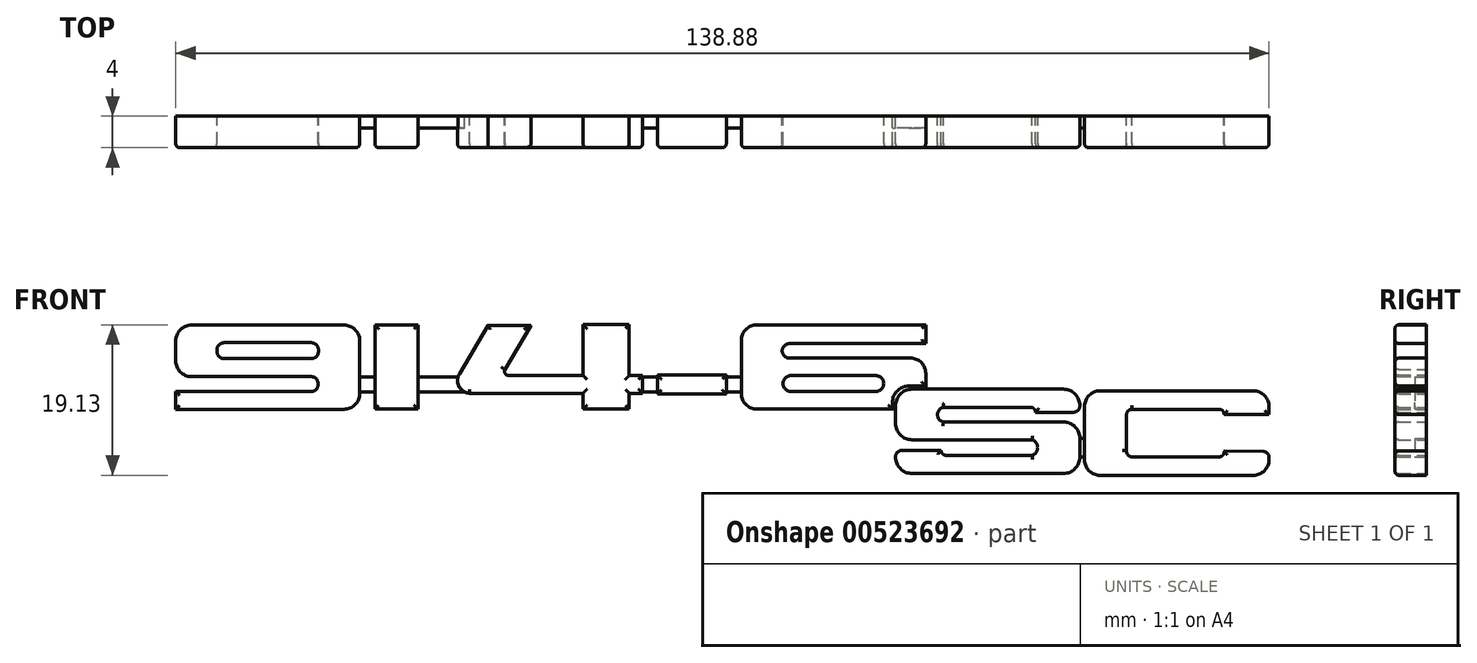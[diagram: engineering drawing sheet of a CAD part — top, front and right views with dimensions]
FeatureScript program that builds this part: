
annotation { "Feature Type Name" : "Feature", "Feature Type Description" : "" }
export const myFeature = defineFeature(function(context is Context, id is Id, definition is map)
    precondition{}
    {
        {
            var Q0;
            Q0=qCreatedBy(makeId("Front.planeOp"),FACE);
            var sketch = newSketch(context, id + "F0", { "sketchPlane" : qUnion([Q0])});
            skLineSegment(sketch, "E0.bottom", {"start": v(-66.52, 34.25) * mm, "end": v(-47.14, 34.25) * mm});
            skLineSegment(sketch, "E0.top", {"start": v(-68.52, 23.57) * mm, "end": v(-47.14, 23.57) * mm});
            skLineSegment(sketch, "E0.left", {"start": v(-68.52, 32.25) * mm, "end": v(-68.52, 29.72) * mm});
            skLineSegment(sketch, "E0.right", {"start": v(-45.14, 32.25) * mm, "end": v(-45.14, 25.57) * mm});
            skPoint(sketch, "E1.visualSharp", {"position": v(-68.52, 34.25) * mm});
            skArc(sketch, "E1.filletArc", {"start": v(-66.52, 34.25) * mm, "mid": v(-67.93, 33.67) * mm, "end": v(-68.52, 32.25) * mm});
            skLineSegment(sketch, "E2", {"start": v(-66.52, 27.72) * mm, "end": v(-51.34, 27.72) * mm});
            skLineSegment(sketch, "E3", {"start": v(-50.44, 26.81) * mm, "end": v(-50.44, 26.71) * mm});
            skLineSegment(sketch, "E4", {"start": v(-51.34, 25.81) * mm, "end": v(-68.52, 25.81) * mm});
            skLineSegment(sketch, "E5.bottom", {"start": v(-62.39, 32.02) * mm, "end": v(-51.29, 32.02) * mm});
            skLineSegment(sketch, "E5.top", {"start": v(-62.39, 30) * mm, "end": v(-51.29, 30) * mm});
            skLineSegment(sketch, "E5.left", {"start": v(-63.3, 31.12) * mm, "end": v(-63.3, 30.91) * mm});
            skLineSegment(sketch, "E5.right", {"start": v(-50.39, 31.12) * mm, "end": v(-50.39, 30.91) * mm});
            skLineSegment(sketch, "E6.trimOffspring", {"start": v(-68.52, 25.81) * mm, "end": v(-68.52, 23.57) * mm});
            skPoint(sketch, "E7.visualSharp", {"position": v(-68.52, 27.72) * mm});
            skArc(sketch, "E7.filletArc", {"start": v(-68.52, 29.72) * mm, "mid": v(-67.93, 28.3) * mm, "end": v(-66.52, 27.72) * mm});
            skPoint(sketch, "E8.visualSharp", {"position": v(-50.44, 27.72) * mm});
            skArc(sketch, "E8.filletArc", {"start": v(-50.44, 26.81) * mm, "mid": v(-50.7, 27.45) * mm, "end": v(-51.34, 27.72) * mm});
            skPoint(sketch, "E9.visualSharp", {"position": v(-50.44, 25.81) * mm});
            skArc(sketch, "E9.filletArc", {"start": v(-51.34, 25.81) * mm, "mid": v(-50.7, 26.08) * mm, "end": v(-50.44, 26.71) * mm});
            skPoint(sketch, "E10.visualSharp", {"position": v(-63.3, 32.02) * mm});
            skArc(sketch, "E10.filletArc", {"start": v(-62.39, 32.02) * mm, "mid": v(-63.03, 31.75) * mm, "end": v(-63.3, 31.12) * mm});
            skPoint(sketch, "E11.visualSharp", {"position": v(-63.3, 30) * mm});
            skArc(sketch, "E11.filletArc", {"start": v(-63.3, 30.91) * mm, "mid": v(-63.03, 30.27) * mm, "end": v(-62.39, 30) * mm});
            skPoint(sketch, "E12.visualSharp", {"position": v(-50.39, 32.02) * mm});
            skArc(sketch, "E12.filletArc", {"start": v(-50.39, 31.12) * mm, "mid": v(-50.65, 31.75) * mm, "end": v(-51.29, 32.02) * mm});
            skPoint(sketch, "E13.visualSharp", {"position": v(-50.39, 30) * mm});
            skArc(sketch, "E13.filletArc", {"start": v(-51.29, 30) * mm, "mid": v(-50.65, 30.27) * mm, "end": v(-50.39, 30.91) * mm});
            skPoint(sketch, "E14.visualSharp", {"position": v(-45.14, 34.25) * mm});
            skArc(sketch, "E14.filletArc", {"start": v(-45.14, 32.25) * mm, "mid": v(-45.72, 33.67) * mm, "end": v(-47.14, 34.25) * mm});
            skPoint(sketch, "E15.visualSharp", {"position": v(-45.14, 23.57) * mm});
            skArc(sketch, "E15.filletArc", {"start": v(-47.14, 23.57) * mm, "mid": v(-45.72, 24.16) * mm, "end": v(-45.14, 25.57) * mm});
            skLineSegment(sketch, "E16.bottom", {"start": v(-43.22, 34.26) * mm, "end": v(-37.74, 34.26) * mm});
            skLineSegment(sketch, "E16.top", {"start": v(-43.22, 23.58) * mm, "end": v(-37.74, 23.58) * mm});
            skLineSegment(sketch, "E16.left", {"start": v(-43.22, 34.26) * mm, "end": v(-43.22, 23.58) * mm});
            skLineSegment(sketch, "E16.right", {"start": v(-37.74, 34.26) * mm, "end": v(-37.74, 23.58) * mm});
            skLineSegment(sketch, "E17.bottom", {"start": v(-10.91, 34.3) * mm, "end": v(-16.77, 34.3) * mm});
            skLineSegment(sketch, "E17.top", {"start": v(-10.91, 23.58) * mm, "end": v(-16.77, 23.58) * mm});
            skLineSegment(sketch, "E17.left", {"start": v(-10.91, 34.3) * mm, "end": v(-10.91, 27.87) * mm});
            skLineSegment(sketch, "E17.right", {"start": v(-16.77, 34.3) * mm, "end": v(-16.77, 27.87) * mm});
            skLineSegment(sketch, "E18.bottom", {"start": v(-9.22, 27.87) * mm, "end": v(-10.91, 27.87) * mm});
            skLineSegment(sketch, "E18.top", {"start": v(-9.22, 25.6) * mm, "end": v(-10.91, 25.6) * mm});
            skLineSegment(sketch, "E18.left", {"start": v(-9.22, 27.87) * mm, "end": v(-9.22, 25.6) * mm});
            skLineSegment(sketch, "E19.trimOffspring", {"start": v(-16.77, 27.87) * mm, "end": v(-26.26, 27.87) * mm});
            skLineSegment(sketch, "E20.trimOffspring", {"start": v(-10.91, 25.6) * mm, "end": v(-10.91, 23.58) * mm});
            skLineSegment(sketch, "E21.trimOffspring", {"start": v(-16.77, 25.6) * mm, "end": v(-26.26, 25.6) * mm});
            skLineSegment(sketch, "E22.trimOffspring", {"start": v(-16.77, 25.6) * mm, "end": v(-16.77, 23.58) * mm});
            skLineSegment(sketch, "E23", {"start": v(-23.37, 34.22) * mm, "end": v(-28.86, 34.22) * mm});
            skLineSegment(sketch, "E24", {"start": v(-23.37, 34.22) * mm, "end": v(-26.68, 28.6) * mm});
            skLineSegment(sketch, "E25", {"start": v(-28.86, 34.22) * mm, "end": v(-32.5, 28.07) * mm});
            skLineSegment(sketch, "E26", {"start": v(-26.26, 25.6) * mm, "end": v(-31.22, 25.6) * mm});
            skArc(sketch, "E27", {"start": v(-32.5, 28.07) * mm, "mid": v(-32.54, 26.48) * mm, "end": v(-31.22, 25.6) * mm});
            skArc(sketch, "E28", {"start": v(-26.68, 28.6) * mm, "mid": v(-26.69, 28.12) * mm, "end": v(-26.26, 27.87) * mm});
            skLineSegment(sketch, "E29.bottom", {"start": v(-7.32, 27.9) * mm, "end": v(1.42, 27.9) * mm});
            skLineSegment(sketch, "E29.top", {"start": v(-7.32, 25.5) * mm, "end": v(1.42, 25.5) * mm});
            skLineSegment(sketch, "E29.left", {"start": v(-7.32, 27.9) * mm, "end": v(-7.32, 25.5) * mm});
            skLineSegment(sketch, "E29.right", {"start": v(1.42, 27.9) * mm, "end": v(1.42, 25.5) * mm});
            skLineSegment(sketch, "E30.bottom", {"start": v(26.75, 34.3) * mm, "end": v(5.33, 34.3) * mm});
            skLineSegment(sketch, "E30.top", {"start": v(22.52, 23.57) * mm, "end": v(5.33, 23.57) * mm});
            skLineSegment(sketch, "E30.left", {"start": v(26.75, 34.3) * mm, "end": v(26.75, 31.9) * mm});
            skLineSegment(sketch, "E30.right", {"start": v(3.33, 32.3) * mm, "end": v(3.33, 25.57) * mm});
            skPoint(sketch, "E31.visualSharp", {"position": v(3.33, 34.3) * mm});
            skArc(sketch, "E31.filletArc", {"start": v(5.33, 34.3) * mm, "mid": v(3.91, 33.71) * mm, "end": v(3.33, 32.3) * mm});
            skPoint(sketch, "E32.visualSharp", {"position": v(3.33, 23.57) * mm});
            skArc(sketch, "E32.filletArc", {"start": v(3.33, 25.57) * mm, "mid": v(3.91, 24.16) * mm, "end": v(5.33, 23.57) * mm});
            skLineSegment(sketch, "E33", {"start": v(26.75, 31.9) * mm, "end": v(9.44, 31.9) * mm});
            skLineSegment(sketch, "E34", {"start": v(9.44, 30.06) * mm, "end": v(24.83, 30.06) * mm});
            skLineSegment(sketch, "E35.bottom", {"start": v(9.61, 27.84) * mm, "end": v(20.42, 27.84) * mm});
            skLineSegment(sketch, "E35.top", {"start": v(9.61, 25.82) * mm, "end": v(20.42, 25.82) * mm});
            skLineSegment(sketch, "E35.left", {"start": v(8.61, 26.84) * mm, "end": v(8.61, 26.82) * mm});
            skLineSegment(sketch, "E35.right", {"start": v(21.42, 26.84) * mm, "end": v(21.42, 26.82) * mm});
            skPoint(sketch, "E36.visualSharp", {"position": v(8.61, 27.84) * mm});
            skArc(sketch, "E36.filletArc", {"start": v(9.61, 27.84) * mm, "mid": v(8.9, 27.54) * mm, "end": v(8.61, 26.84) * mm});
            skPoint(sketch, "E37.visualSharp", {"position": v(8.61, 25.82) * mm});
            skArc(sketch, "E37.filletArc", {"start": v(8.61, 26.82) * mm, "mid": v(8.9, 26.12) * mm, "end": v(9.61, 25.82) * mm});
            skPoint(sketch, "E38.visualSharp", {"position": v(21.42, 27.84) * mm});
            skArc(sketch, "E38.filletArc", {"start": v(21.42, 26.84) * mm, "mid": v(21.13, 27.54) * mm, "end": v(20.42, 27.84) * mm});
            skPoint(sketch, "E39.visualSharp", {"position": v(21.42, 25.82) * mm});
            skArc(sketch, "E39.filletArc", {"start": v(20.42, 25.82) * mm, "mid": v(21.13, 26.12) * mm, "end": v(21.42, 26.82) * mm});
            skArc(sketch, "E40", {"start": v(9.44, 31.9) * mm, "mid": v(8.52, 30.98) * mm, "end": v(9.44, 30.06) * mm});
            skLineSegment(sketch, "E41.trimOffspring", {"start": v(26.75, 28.14) * mm, "end": v(26.75, 26.52) * mm});
            skPoint(sketch, "E42.visualSharp", {"position": v(26.75, 30.06) * mm});
            skArc(sketch, "E42.filletArc", {"start": v(26.75, 28.14) * mm, "mid": v(26.19, 29.5) * mm, "end": v(24.83, 30.06) * mm});
            skLineSegment(sketch, "E43", {"start": v(22.52, 23.57) * mm, "end": v(22.52, 24.42) * mm});
            skLineSegment(sketch, "E44", {"start": v(24.62, 26.52) * mm, "end": v(26.75, 26.52) * mm});
            skPoint(sketch, "E45.visualSharp", {"position": v(22.52, 26.52) * mm});
            skArc(sketch, "E45.filletArc", {"start": v(24.62, 26.52) * mm, "mid": v(23.13, 25.9) * mm, "end": v(22.52, 24.42) * mm});
            skPoint(sketch, "E46.firstSnap0", {"position": v(21.13, 26.12) * mm});
            skLineSegment(sketch, "E46.bottom", {"start": v(44.24, 26.12) * mm, "end": v(25.02, 26.12) * mm});
            skLineSegment(sketch, "E46.top", {"start": v(44.24, 15.4) * mm, "end": v(25.02, 15.4) * mm});
            skLineSegment(sketch, "E46.left", {"start": v(46.34, 24.02) * mm, "end": v(46.34, 24.02) * mm});
            skLineSegment(sketch, "E46.right", {"start": v(22.92, 24.02) * mm, "end": v(22.92, 21.78) * mm});
            skPoint(sketch, "E47.visualSharp", {"position": v(22.92, 26.12) * mm});
            skArc(sketch, "E47.filletArc", {"start": v(25.02, 26.12) * mm, "mid": v(23.53, 25.5) * mm, "end": v(22.92, 24.02) * mm});
            skPoint(sketch, "E48.visualSharp", {"position": v(46.34, 26.12) * mm});
            skArc(sketch, "E48.filletArc", {"start": v(46.34, 24.02) * mm, "mid": v(45.72, 25.5) * mm, "end": v(44.24, 26.12) * mm});
            skPoint(sketch, "E49.visualSharp", {"position": v(46.34, 15.4) * mm});
            skArc(sketch, "E49.filletArc", {"start": v(44.24, 15.4) * mm, "mid": v(45.72, 16.01) * mm, "end": v(46.34, 17.5) * mm});
            skPoint(sketch, "E50.visualSharp", {"position": v(22.92, 15.4) * mm});
            skArc(sketch, "E50.filletArc", {"start": v(22.92, 17.5) * mm, "mid": v(23.53, 16.01) * mm, "end": v(25.02, 15.4) * mm});
            skLineSegment(sketch, "E51", {"start": v(25, 19.69) * mm, "end": v(40.26, 19.69) * mm});
            skLineSegment(sketch, "E52", {"start": v(40.26, 17.72) * mm, "end": v(29.31, 17.72) * mm});
            skLineSegment(sketch, "E53", {"start": v(28.71, 18.36) * mm, "end": v(23.76, 18.36) * mm});
            skLineSegment(sketch, "E54", {"start": v(29, 21.95) * mm, "end": v(44.25, 21.95) * mm});
            skLineSegment(sketch, "E55", {"start": v(45.5, 23.18) * mm, "end": v(40.69, 23.18) * mm});
            skLineSegment(sketch, "E56", {"start": v(40.09, 23.81) * mm, "end": v(29.01, 23.81) * mm});
            skArc(sketch, "E57", {"start": v(29.01, 23.81) * mm, "mid": v(28.25, 22.9) * mm, "end": v(29, 21.95) * mm});
            skArc(sketch, "E58", {"start": v(40.26, 17.72) * mm, "mid": v(40.97, 18.7) * mm, "end": v(40.26, 19.69) * mm});
            skPoint(sketch, "E59.end.orphan", {"position": v(40.69, 23.81) * mm});
            skArc(sketch, "E60", {"start": v(40.69, 23.18) * mm, "mid": v(40.52, 23.62) * mm, "end": v(40.09, 23.81) * mm});
            skArc(sketch, "E61", {"start": v(28.71, 18.36) * mm, "mid": v(28.87, 17.9) * mm, "end": v(29.31, 17.72) * mm});
            skLineSegment(sketch, "E62.trimOffspring", {"start": v(22.92, 17.51) * mm, "end": v(22.92, 17.5) * mm});
            skPoint(sketch, "E63.visualSharp", {"position": v(22.92, 18.36) * mm});
            skArc(sketch, "E63.filletArc", {"start": v(23.76, 18.36) * mm, "mid": v(23.17, 18.1) * mm, "end": v(22.92, 17.51) * mm});
            skPoint(sketch, "E64.visualSharp", {"position": v(22.92, 19.69) * mm});
            skArc(sketch, "E64.filletArc", {"start": v(22.92, 21.78) * mm, "mid": v(23.53, 20.3) * mm, "end": v(25, 19.69) * mm});
            skLineSegment(sketch, "E65.trimOffspring", {"start": v(46.34, 19.87) * mm, "end": v(46.34, 17.5) * mm});
            skPoint(sketch, "E66.visualSharp", {"position": v(46.34, 23.18) * mm});
            skArc(sketch, "E66.filletArc", {"start": v(45.5, 23.18) * mm, "mid": v(46.1, 23.42) * mm, "end": v(46.34, 24.02) * mm});
            skPoint(sketch, "E67.visualSharp", {"position": v(46.34, 21.95) * mm});
            skArc(sketch, "E67.filletArc", {"start": v(46.34, 19.87) * mm, "mid": v(45.73, 21.34) * mm, "end": v(44.25, 21.95) * mm});
            skLineSegment(sketch, "E68.bottom", {"start": v(48.9, 25.9) * mm, "end": v(68.37, 25.9) * mm});
            skLineSegment(sketch, "E68.top", {"start": v(48.9, 15.17) * mm, "end": v(68.37, 15.17) * mm});
            skLineSegment(sketch, "E68.left", {"start": v(46.92, 23.92) * mm, "end": v(46.92, 17.15) * mm});
            skLineSegment(sketch, "E68.right", {"start": v(70.36, 23.92) * mm, "end": v(70.36, 22.89) * mm});
            skLineSegment(sketch, "E69.bottom", {"start": v(64.02, 23.57) * mm, "end": v(52.96, 23.57) * mm});
            skLineSegment(sketch, "E69.top", {"start": v(64.02, 17.52) * mm, "end": v(52.96, 17.52) * mm});
            skLineSegment(sketch, "E70", {"start": v(70.36, 22.89) * mm, "end": v(64.65, 22.89) * mm});
            skLineSegment(sketch, "E71", {"start": v(69.67, 18.18) * mm, "end": v(64.65, 18.25) * mm});
            skLineSegment(sketch, "E72", {"start": v(52.27, 18.41) * mm, "end": v(52.27, 22.89) * mm});
            skLineSegment(sketch, "E73.trimOffspring", {"start": v(70.36, 17.49) * mm, "end": v(70.36, 17.15) * mm});
            skArc(sketch, "E74", {"start": v(64.65, 22.89) * mm, "mid": v(64.49, 23.37) * mm, "end": v(64.02, 23.57) * mm});
            skArc(sketch, "E75", {"start": v(64.02, 17.52) * mm, "mid": v(64.5, 17.74) * mm, "end": v(64.65, 18.25) * mm});
            skPoint(sketch, "E76.visualSharp", {"position": v(70.36, 18.17) * mm});
            skArc(sketch, "E76.filletArc", {"start": v(70.36, 17.49) * mm, "mid": v(70.16, 17.97) * mm, "end": v(69.67, 18.18) * mm});
            skPoint(sketch, "E77.visualSharp", {"position": v(70.36, 15.17) * mm});
            skArc(sketch, "E77.filletArc", {"start": v(68.37, 15.17) * mm, "mid": v(69.78, 15.75) * mm, "end": v(70.36, 17.15) * mm});
            skPoint(sketch, "E78.visualSharp", {"position": v(70.36, 25.9) * mm});
            skArc(sketch, "E78.filletArc", {"start": v(70.36, 23.92) * mm, "mid": v(69.78, 25.32) * mm, "end": v(68.37, 25.9) * mm});
            skPoint(sketch, "E79.visualSharp", {"position": v(46.92, 25.9) * mm});
            skArc(sketch, "E79.filletArc", {"start": v(48.9, 25.9) * mm, "mid": v(47.5, 25.32) * mm, "end": v(46.92, 23.92) * mm});
            skPoint(sketch, "E80.visualSharp", {"position": v(46.92, 15.17) * mm});
            skArc(sketch, "E80.filletArc", {"start": v(46.92, 17.15) * mm, "mid": v(47.5, 15.75) * mm, "end": v(48.9, 15.17) * mm});
            skArc(sketch, "E81", {"start": v(52.96, 23.57) * mm, "mid": v(52.47, 23.37) * mm, "end": v(52.27, 22.89) * mm});
            skLineSegment(sketch, "E82", {"start": v(52.27, 18.41) * mm, "end": v(52.27, 18.3) * mm});
            skArc(sketch, "E83", {"start": v(52.27, 18.3) * mm, "mid": v(52.44, 17.75) * mm, "end": v(52.96, 17.52) * mm});
            skLineSegment(sketch, "E84", {"start": v(22.52, 23.57) * mm, "end": v(22.92, 23.57) * mm});
            skLineSegment(sketch, "E85", {"start": v(26.75, 26.52) * mm, "end": v(26.75, 26.12) * mm});
            skLineSegment(sketch, "E86.bottom", {"start": v(3.33, 27.64) * mm, "end": v(1.42, 27.64) * mm});
            skLineSegment(sketch, "E86.top", {"start": v(3.33, 25.76) * mm, "end": v(1.42, 25.76) * mm});
            skLineSegment(sketch, "E86.left", {"start": v(3.33, 27.64) * mm, "end": v(3.33, 25.76) * mm});
            skLineSegment(sketch, "E87.trimOffspring", {"start": v(-7.32, 27.64) * mm, "end": v(-9.22, 27.64) * mm});
            skLineSegment(sketch, "E88.trimOffspring", {"start": v(-7.32, 25.76) * mm, "end": v(-9.22, 25.76) * mm});
            skLineSegment(sketch, "E89", {"start": v(-31.8, 25.76) * mm, "end": v(-33.56, 25.76) * mm});
            skLineSegment(sketch, "E90", {"start": v(-32.67, 27.64) * mm, "end": v(-33.56, 27.64) * mm});
            skLineSegment(sketch, "E91", {"start": v(-33.56, 27.64) * mm, "end": v(-37.74, 27.64) * mm});
            skLineSegment(sketch, "E92", {"start": v(-33.56, 25.76) * mm, "end": v(-37.74, 25.76) * mm});
            skLineSegment(sketch, "E93.trimOffspring", {"start": v(-43.22, 27.64) * mm, "end": v(-45.14, 27.64) * mm});
            skLineSegment(sketch, "E94.trimOffspring", {"start": v(-43.22, 25.76) * mm, "end": v(-45.14, 25.76) * mm});
            skLineSegment(sketch, "E95", {"start": v(46.34, 17.5) * mm, "end": v(46.92, 17.5) * mm});
            skLineSegment(sketch, "E96", {"start": v(46.34, 19.87) * mm, "end": v(46.92, 19.87) * mm});
            skSolve(sketch);
        }
        {
            var Q0;
            {var subQ0=sQuery(id+"F0.wireOp",EDGE,"E93.trimOffspring");Q0=makeQuery(id+"F0.imprint","IMPRINT",FACE,{"disambiguationData":[TD([[makeQuery(id+"F0.imprint","IMPRINT",EDGE,{"derivedFrom":subQ0}),1.0]])]});}
            var Q1;
            {var subQ1=sQuery(id+"F0.wireOp",EDGE,"E89");Q1=makeQuery(id+"F0.imprint","IMPRINT",FACE,{"disambiguationData":[TD([[makeQuery(id+"F0.imprint","IMPRINT",EDGE,{"derivedFrom":subQ1}),-1.0]])]});}
            var Q2;
            {var subQ0=sQuery(id+"F0.wireOp",EDGE,"E87.trimOffspring");Q2=makeQuery(id+"F0.imprint","IMPRINT",FACE,{"disambiguationData":[TD([[makeQuery(id+"F0.imprint","IMPRINT",EDGE,{"derivedFrom":subQ0}),1.0]])]});}
            var Q3;
            {var subQ0=sQuery(id+"F0.wireOp",EDGE,"E86.bottom");Q3=makeQuery(id+"F0.imprint","IMPRINT",FACE,{"disambiguationData":[TD([[makeQuery(id+"F0.imprint","IMPRINT",EDGE,{"derivedFrom":subQ0}),1.0]])]});}
            var Q4;
            Q4=makeQuery(id+"F0.imprint","IMPRINT",FACE,{"disambiguationData":[TD([[makeQuery(id+"F0.imprint","IMPRINT",EDGE,{"derivedFrom":sQuery(id+"F0.wireOp",EDGE,"E43")}),-1.0]])]});
            var Q5;
            Q5=makeQuery(id+"F0.imprint","IMPRINT",FACE,{"disambiguationData":[TD([[makeQuery(id+"F0.imprint","IMPRINT",EDGE,{"derivedFrom":sQuery(id+"F0.wireOp",EDGE,"E65.trimOffspring")}),1.0]])]});
            extrude(context, id + "F1", {"entities" : qUnion([Q0, Q1, Q2, Q3, Q4, Q5]), "depth" : 1.5 * mm, "offsetDistance" : 25 * mm});
        }
        {
            var Q0;
            Q0=makeQuery(id+"F0.imprint","IMPRINT",FACE,{"disambiguationData":[TD([[makeQuery(id+"F0.imprint","IMPRINT",EDGE,{"derivedFrom":sQuery(id+"F0.wireOp",EDGE,"E0.bottom")}),-1.0]])]});
            var Q1;
            {var subQ3=sQuery(id+"F0.wireOp",EDGE,"E16.bottom");Q1=makeQuery(id+"F0.imprint","IMPRINT",FACE,{"disambiguationData":[TD([[makeQuery(id+"F0.imprint","IMPRINT",EDGE,{"derivedFrom":subQ3}),-1.0]])]});}
            var Q2;
            Q2=makeQuery(id+"F0.imprint","IMPRINT",FACE,{"disambiguationData":[TD([[makeQuery(id+"F0.imprint","IMPRINT",EDGE,{"derivedFrom":sQuery(id+"F0.wireOp",EDGE,"E17.bottom")}),1.0]])]});
            var Q3;
            {var subQ3=sQuery(id+"F0.wireOp",EDGE,"E29.bottom");Q3=makeQuery(id+"F0.imprint","IMPRINT",FACE,{"disambiguationData":[TD([[makeQuery(id+"F0.imprint","IMPRINT",EDGE,{"derivedFrom":subQ3}),-1.0]])]});}
            var Q4;
            Q4=makeQuery(id+"F0.imprint","IMPRINT",FACE,{"disambiguationData":[TD([[makeQuery(id+"F0.imprint","IMPRINT",EDGE,{"derivedFrom":sQuery(id+"F0.wireOp",EDGE,"E30.bottom")}),1.0]])]});
            var Q5;
            Q5=makeQuery(id+"F0.imprint","IMPRINT",FACE,{"disambiguationData":[TD([[makeQuery(id+"F0.imprint","IMPRINT",EDGE,{"derivedFrom":sQuery(id+"F0.wireOp",EDGE,"E46.top")}),-1.0]])]});
            var Q6;
            Q6=makeQuery(id+"F0.imprint","IMPRINT",FACE,{"disambiguationData":[TD([[makeQuery(id+"F0.imprint","IMPRINT",EDGE,{"derivedFrom":sQuery(id+"F0.wireOp",EDGE,"E68.bottom")}),-1.0]])]});
            extrude(context, id + "F2", {"entities" : qUnion([Q0, Q1, Q2, Q3, Q4, Q5, Q6]), "depth" : 4 * mm, "offsetDistance" : 25 * mm});
        }
        {
            var Q0;
            Q0=makeQuery(id+"F2.opExtrude","CAP_FACE",FACE,{"disambiguationData":[OSD([sQuery(id+"F0.wireOp",EDGE,"E0.bottom"),sQuery(id+"F0.wireOp",EDGE,"E0.top"),sQuery(id+"F0.wireOp",EDGE,"E0.left"),sQuery(id+"F0.wireOp",EDGE,"E0.right"),sQuery(id+"F0.wireOp",EDGE,"E1.filletArc"),sQuery(id+"F0.wireOp",EDGE,"E2"),sQuery(id+"F0.wireOp",EDGE,"E3"),sQuery(id+"F0.wireOp",EDGE,"E4"),sQuery(id+"F0.wireOp",EDGE,"E5.bottom"),sQuery(id+"F0.wireOp",EDGE,"E5.top"),sQuery(id+"F0.wireOp",EDGE,"E5.left"),sQuery(id+"F0.wireOp",EDGE,"E5.right"),sQuery(id+"F0.wireOp",EDGE,"E6.trimOffspring"),sQuery(id+"F0.wireOp",EDGE,"E7.filletArc"),sQuery(id+"F0.wireOp",EDGE,"E8.filletArc"),sQuery(id+"F0.wireOp",EDGE,"E9.filletArc"),sQuery(id+"F0.wireOp",EDGE,"E10.filletArc"),sQuery(id+"F0.wireOp",EDGE,"E11.filletArc"),sQuery(id+"F0.wireOp",EDGE,"E12.filletArc"),sQuery(id+"F0.wireOp",EDGE,"E13.filletArc"),sQuery(id+"F0.wireOp",EDGE,"E14.filletArc"),sQuery(id+"F0.wireOp",EDGE,"E15.filletArc")])],"isStart":false});
            var Q1;
            Q1=makeQuery(id+"F2.opExtrude","CAP_FACE",FACE,{"disambiguationData":[OSD([sQuery(id+"F0.wireOp",EDGE,"E16.bottom"),sQuery(id+"F0.wireOp",EDGE,"E16.top"),sQuery(id+"F0.wireOp",EDGE,"E16.left"),sQuery(id+"F0.wireOp",EDGE,"E16.right")])],"isStart":false});
            var Q2;
            Q2=makeQuery(id+"F2.opExtrude","CAP_FACE",FACE,{"disambiguationData":[OSD([sQuery(id+"F0.wireOp",EDGE,"E17.bottom"),sQuery(id+"F0.wireOp",EDGE,"E17.top"),sQuery(id+"F0.wireOp",EDGE,"E17.left"),sQuery(id+"F0.wireOp",EDGE,"E17.right"),sQuery(id+"F0.wireOp",EDGE,"E18.bottom"),sQuery(id+"F0.wireOp",EDGE,"E18.top"),sQuery(id+"F0.wireOp",EDGE,"E18.left"),sQuery(id+"F0.wireOp",EDGE,"E19.trimOffspring"),sQuery(id+"F0.wireOp",EDGE,"E20.trimOffspring"),sQuery(id+"F0.wireOp",EDGE,"E21.trimOffspring"),sQuery(id+"F0.wireOp",EDGE,"E22.trimOffspring"),sQuery(id+"F0.wireOp",EDGE,"E23"),sQuery(id+"F0.wireOp",EDGE,"E24"),sQuery(id+"F0.wireOp",EDGE,"E25"),sQuery(id+"F0.wireOp",EDGE,"E26"),sQuery(id+"F0.wireOp",EDGE,"E27"),sQuery(id+"F0.wireOp",EDGE,"E28")])],"isStart":false});
            var Q3;
            Q3=makeQuery(id+"F2.opExtrude","CAP_FACE",FACE,{"disambiguationData":[OSD([sQuery(id+"F0.wireOp",EDGE,"E29.bottom"),sQuery(id+"F0.wireOp",EDGE,"E29.top"),sQuery(id+"F0.wireOp",EDGE,"E29.left"),sQuery(id+"F0.wireOp",EDGE,"E29.right")])],"isStart":false});
            var Q4;
            Q4=makeQuery(id+"F2.opExtrude","CAP_FACE",FACE,{"disambiguationData":[OSD([sQuery(id+"F0.wireOp",EDGE,"E30.bottom"),sQuery(id+"F0.wireOp",EDGE,"E30.top"),sQuery(id+"F0.wireOp",EDGE,"E30.left"),sQuery(id+"F0.wireOp",EDGE,"E30.right"),sQuery(id+"F0.wireOp",EDGE,"E31.filletArc"),sQuery(id+"F0.wireOp",EDGE,"E32.filletArc"),sQuery(id+"F0.wireOp",EDGE,"E33"),sQuery(id+"F0.wireOp",EDGE,"E34"),sQuery(id+"F0.wireOp",EDGE,"E35.bottom"),sQuery(id+"F0.wireOp",EDGE,"E35.top"),sQuery(id+"F0.wireOp",EDGE,"E35.left"),sQuery(id+"F0.wireOp",EDGE,"E35.right"),sQuery(id+"F0.wireOp",EDGE,"E36.filletArc"),sQuery(id+"F0.wireOp",EDGE,"E37.filletArc"),sQuery(id+"F0.wireOp",EDGE,"E38.filletArc"),sQuery(id+"F0.wireOp",EDGE,"E39.filletArc"),sQuery(id+"F0.wireOp",EDGE,"E40"),sQuery(id+"F0.wireOp",EDGE,"E41.trimOffspring"),sQuery(id+"F0.wireOp",EDGE,"E42.filletArc"),sQuery(id+"F0.wireOp",EDGE,"E43"),sQuery(id+"F0.wireOp",EDGE,"E44"),sQuery(id+"F0.wireOp",EDGE,"E45.filletArc"),sQuery(id+"F0.wireOp",EDGE,"E86.left")])],"isStart":false});
            var Q5;
            Q5=makeQuery(id+"F2.opExtrude","CAP_FACE",FACE,{"disambiguationData":[OSD([sQuery(id+"F0.wireOp",EDGE,"E46.bottom"),sQuery(id+"F0.wireOp",EDGE,"E46.top"),sQuery(id+"F0.wireOp",EDGE,"E46.left"),sQuery(id+"F0.wireOp",EDGE,"E46.right"),sQuery(id+"F0.wireOp",EDGE,"E47.filletArc"),sQuery(id+"F0.wireOp",EDGE,"E48.filletArc"),sQuery(id+"F0.wireOp",EDGE,"E49.filletArc"),sQuery(id+"F0.wireOp",EDGE,"E50.filletArc"),sQuery(id+"F0.wireOp",EDGE,"E51"),sQuery(id+"F0.wireOp",EDGE,"E52"),sQuery(id+"F0.wireOp",EDGE,"E53"),sQuery(id+"F0.wireOp",EDGE,"E54"),sQuery(id+"F0.wireOp",EDGE,"E55"),sQuery(id+"F0.wireOp",EDGE,"E56"),sQuery(id+"F0.wireOp",EDGE,"E57"),sQuery(id+"F0.wireOp",EDGE,"E58"),sQuery(id+"F0.wireOp",EDGE,"E60"),sQuery(id+"F0.wireOp",EDGE,"E61"),sQuery(id+"F0.wireOp",EDGE,"E62.trimOffspring"),sQuery(id+"F0.wireOp",EDGE,"E63.filletArc"),sQuery(id+"F0.wireOp",EDGE,"E64.filletArc"),sQuery(id+"F0.wireOp",EDGE,"E65.trimOffspring"),sQuery(id+"F0.wireOp",EDGE,"E66.filletArc"),sQuery(id+"F0.wireOp",EDGE,"E67.filletArc")])],"isStart":false});
            var Q6;
            Q6=makeQuery(id+"F2.opExtrude","CAP_FACE",FACE,{"disambiguationData":[OSD([sQuery(id+"F0.wireOp",EDGE,"E68.bottom"),sQuery(id+"F0.wireOp",EDGE,"E68.top"),sQuery(id+"F0.wireOp",EDGE,"E68.left"),sQuery(id+"F0.wireOp",EDGE,"E68.right"),sQuery(id+"F0.wireOp",EDGE,"E69.bottom"),sQuery(id+"F0.wireOp",EDGE,"E69.top"),sQuery(id+"F0.wireOp",EDGE,"E70"),sQuery(id+"F0.wireOp",EDGE,"E71"),sQuery(id+"F0.wireOp",EDGE,"E72"),sQuery(id+"F0.wireOp",EDGE,"E73.trimOffspring"),sQuery(id+"F0.wireOp",EDGE,"E74"),sQuery(id+"F0.wireOp",EDGE,"E75"),sQuery(id+"F0.wireOp",EDGE,"E76.filletArc"),sQuery(id+"F0.wireOp",EDGE,"E77.filletArc"),sQuery(id+"F0.wireOp",EDGE,"E78.filletArc"),sQuery(id+"F0.wireOp",EDGE,"E79.filletArc"),sQuery(id+"F0.wireOp",EDGE,"E80.filletArc"),sQuery(id+"F0.wireOp",EDGE,"E81"),sQuery(id+"F0.wireOp",EDGE,"E82"),sQuery(id+"F0.wireOp",EDGE,"E83")])],"isStart":false});
            fillet(context, id + "F3", {"entities" : qUnion([Q0, Q1, Q2, Q3, Q4, Q5, Q6]), "radius" : .5 * mm, "tangentPropagation" : true, "allowEdgeOverflow" : false});
        }
    });
